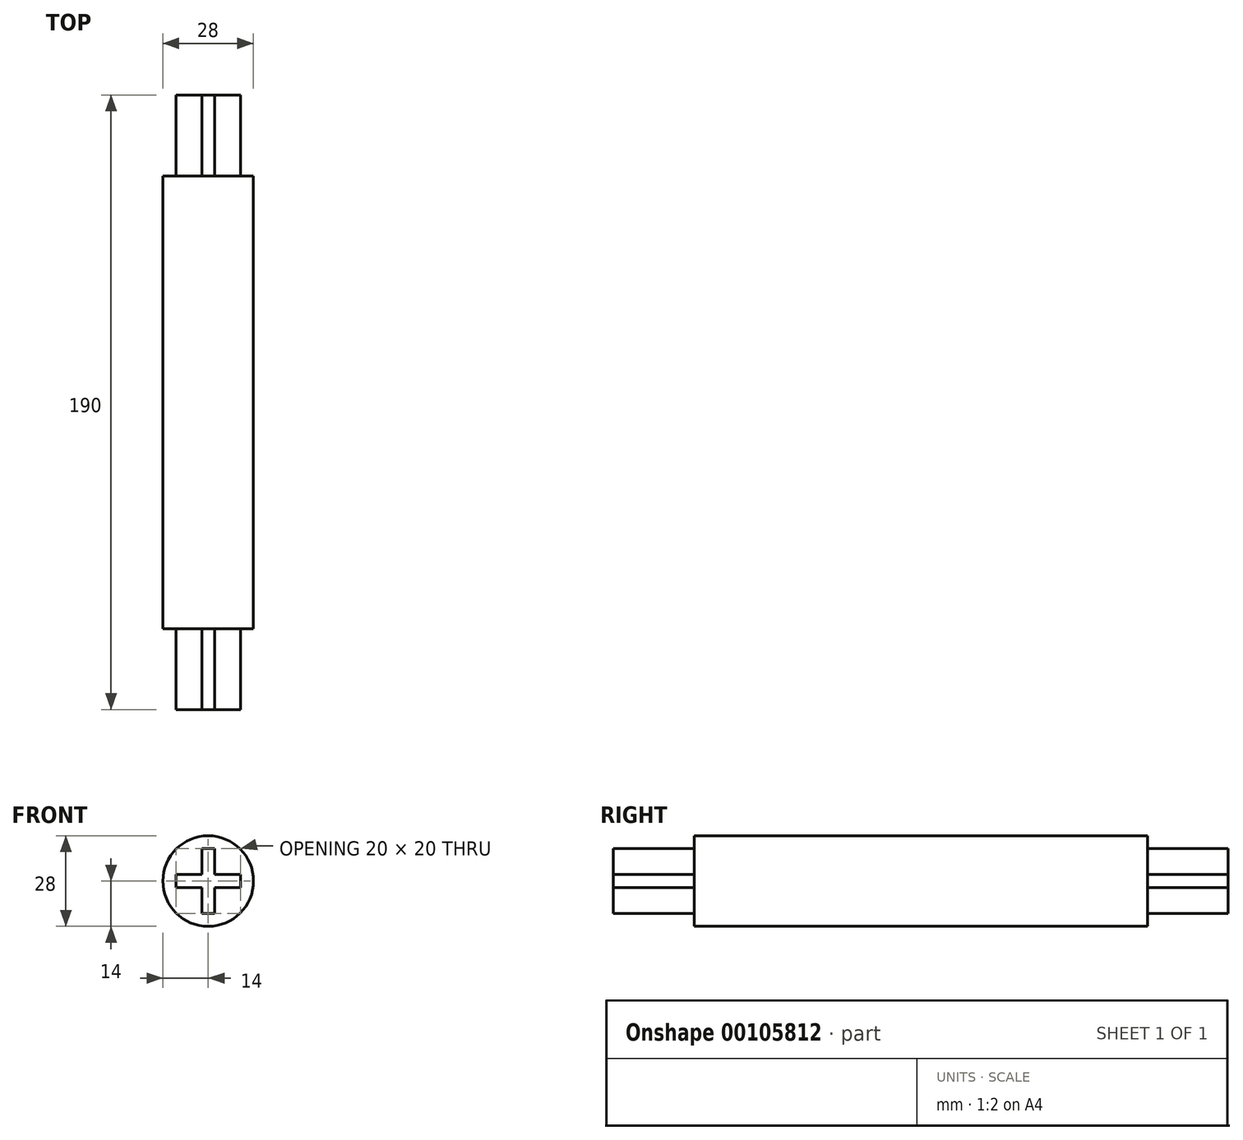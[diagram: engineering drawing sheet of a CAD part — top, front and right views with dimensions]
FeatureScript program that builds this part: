
annotation { "Feature Type Name" : "Feature", "Feature Type Description" : "" }
export const myFeature = defineFeature(function(context is Context, id is Id, definition is map)
    precondition{}
    {
        {
            var Q0;
            Q0=qCreatedBy(makeId("Front.planeOp"),FACE);
            var sketch = newSketch(context, id + "F0", { "sketchPlane" : qUnion([Q0])});
            skCircle(sketch, "E0", {"center": v(0, 0) * mm, "radius": 14 * mm});
            skSolve(sketch);
        }
        {
            var Q0;
            Q0=makeQuery(id+"F0.imprint","IMPRINT",FACE,{"disambiguationData":[TD([[makeQuery(id+"F0.imprint","IMPRINT",EDGE,{"derivedFrom":sQuery(id+"F0.wireOp",EDGE,"E0")}),1.0]])]});
            extrude(context, id + "F1", {"entities" : qUnion([Q0]), "depth" : 140 * mm});
        }
        {
            var Q0;
            Q0=qCreatedBy(makeId("Front.planeOp"),FACE);
            var sketch = newSketch(context, id + "F2", { "sketchPlane" : qUnion([Q0])});
            skLineSegment(sketch, "E1.bottom", {"start": v(-2, 10) * mm, "end": v(2, 10) * mm});
            skLineSegment(sketch, "E1.top", {"start": v(-2, -10) * mm, "end": v(2, -10) * mm});
            skLineSegment(sketch, "E1.left", {"start": v(-2, 10) * mm, "end": v(-2, 2) * mm});
            skLineSegment(sketch, "E1.right", {"start": v(2, 10) * mm, "end": v(2, 2) * mm});
            skPoint(sketch, "E1.middle", {"position": v(0, 0) * mm});
            skLineSegment(sketch, "E2.bottom", {"start": v(-10, 2) * mm, "end": v(-2, 2) * mm});
            skLineSegment(sketch, "E2.top", {"start": v(-10, -2) * mm, "end": v(-2, -2) * mm});
            skLineSegment(sketch, "E2.left", {"start": v(-10, 2) * mm, "end": v(-10, -2) * mm});
            skLineSegment(sketch, "E2.right", {"start": v(10, 2) * mm, "end": v(10, -2) * mm});
            skLineSegment(sketch, "E3.trimOffspring", {"start": v(2, 2) * mm, "end": v(10, 2) * mm});
            skLineSegment(sketch, "E4.trimOffspring", {"start": v(2, -2) * mm, "end": v(2, -10) * mm});
            skLineSegment(sketch, "E5.trimOffspring", {"start": v(2, -2) * mm, "end": v(10, -2) * mm});
            skLineSegment(sketch, "E6.trimOffspring", {"start": v(-2, -2) * mm, "end": v(-2, -10) * mm});
            skSolve(sketch);
        }
        {
            var Q0;
            Q0 = qSketchRegion(id + "F2", true);
            extrude(context, id + "F3", {"entities" : qUnion([Q0]), "operationType" : NewBodyOperationType.ADD, "oppositeDirection" : true, "depth" : 25 * mm});
        }
        {
            var Q0;
            Q0=makeQuery(id+"F1.opExtrude","CAP_FACE",FACE,{"disambiguationData":[OSD([sQuery(id+"F0.wireOp",EDGE,"E0")])],"isStart":false});
            var sketch = newSketch(context, id + "F4", { "sketchPlane" : qUnion([Q0])});
            skLineSegment(sketch, "E7.bottom", {"start": v(-10, 2) * mm, "end": v(-2, 2) * mm});
            skLineSegment(sketch, "E7.top", {"start": v(-10, -2) * mm, "end": v(-2, -2) * mm});
            skLineSegment(sketch, "E7.left", {"start": v(-10, 2) * mm, "end": v(-10, -2) * mm});
            skLineSegment(sketch, "E7.right", {"start": v(10, 2) * mm, "end": v(10, -2) * mm});
            skPoint(sketch, "E7.middle", {"position": v(0, 0) * mm});
            skLineSegment(sketch, "E8.bottom", {"start": v(2, 10) * mm, "end": v(-2, 10) * mm});
            skLineSegment(sketch, "E8.top", {"start": v(2, -10) * mm, "end": v(-2, -10) * mm});
            skLineSegment(sketch, "E8.left", {"start": v(2, 10) * mm, "end": v(2, 2) * mm});
            skLineSegment(sketch, "E8.right", {"start": v(-2, 10) * mm, "end": v(-2, 2) * mm});
            skLineSegment(sketch, "E9.trimOffspring", {"start": v(2, 2) * mm, "end": v(10, 2) * mm});
            skLineSegment(sketch, "E10.trimOffspring", {"start": v(2, -2) * mm, "end": v(2, -10) * mm});
            skLineSegment(sketch, "E11.trimOffspring", {"start": v(2, -2) * mm, "end": v(10, -2) * mm});
            skLineSegment(sketch, "E12.trimOffspring", {"start": v(-2, -2) * mm, "end": v(-2, -10) * mm});
            skSolve(sketch);
        }
        {
            var Q0;
            Q0 = qSketchRegion(id + "F4", true);
            extrude(context, id + "F5", {"entities" : qUnion([Q0]), "operationType" : NewBodyOperationType.ADD, "depth" : 25 * mm});
        }
    });
